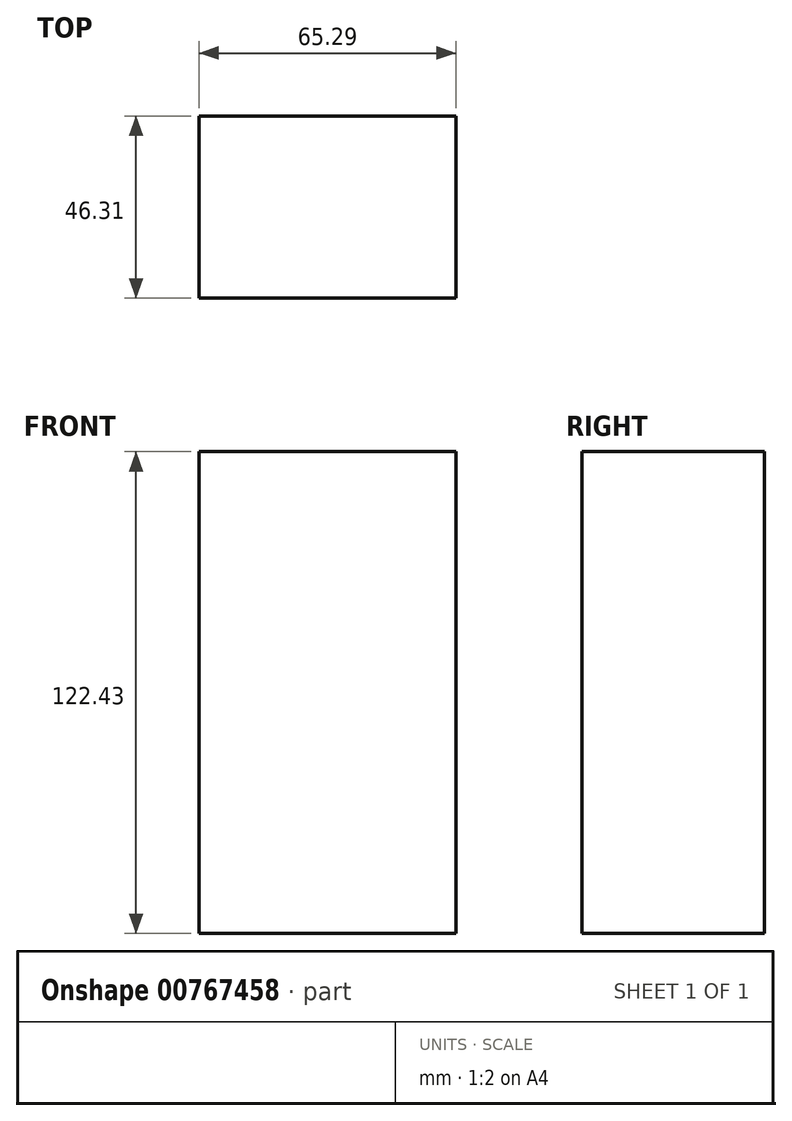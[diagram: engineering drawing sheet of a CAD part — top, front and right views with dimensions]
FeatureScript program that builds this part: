
annotation { "Feature Type Name" : "Feature", "Feature Type Description" : "" }
export const myFeature = defineFeature(function(context is Context, id is Id, definition is map)
    precondition{}
    {
        {
            var Q0;
            Q0=qCreatedBy(makeId("Top.planeOp"),FACE);
            var sketch = newSketch(context, id + "F0", { "sketchPlane" : qUnion([Q0])});
            skLineSegment(sketch, "E0.bottom", {"start": v(-96.23, 55.04) * mm, "end": v(-30.94, 55.04) * mm});
            skLineSegment(sketch, "E0.top", {"start": v(-96.23, 8.73) * mm, "end": v(-30.94, 8.73) * mm});
            skLineSegment(sketch, "E0.left", {"start": v(-96.23, 55.04) * mm, "end": v(-96.23, 8.73) * mm});
            skLineSegment(sketch, "E0.right", {"start": v(-30.94, 55.04) * mm, "end": v(-30.94, 8.73) * mm});
            skSolve(sketch);
        }
        {
            var Q0;
            Q0=makeQuery(id+"F0.imprint","IMPRINT",FACE,{"disambiguationData":[TD([[makeQuery(id+"F0.imprint","IMPRINT",EDGE,{"derivedFrom":sQuery(id+"F0.wireOp",EDGE,"E0.bottom")}),-1.0]])]});
            extrude(context, id + "F1", {"entities" : qUnion([Q0]), "depth" : 122.43 * mm, "offsetDistance" : 25.4 * mm});
        }
    });
